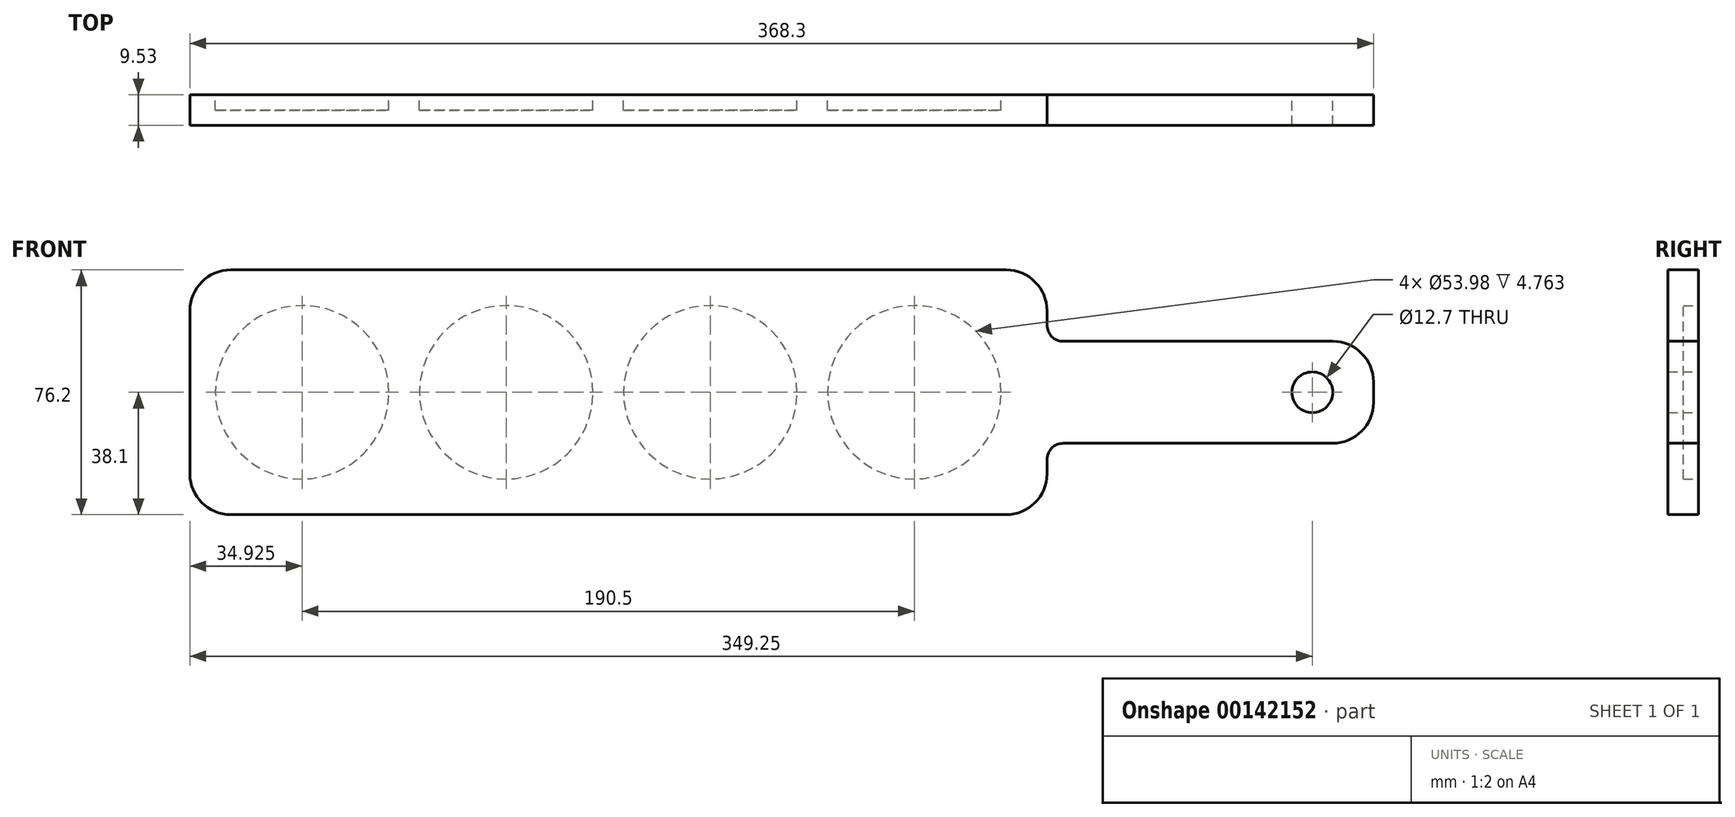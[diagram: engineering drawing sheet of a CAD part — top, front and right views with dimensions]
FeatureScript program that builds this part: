
annotation { "Feature Type Name" : "Feature", "Feature Type Description" : "" }
export const myFeature = defineFeature(function(context is Context, id is Id, definition is map)
    precondition{}
    {
        {
            var Q0;
            Q0=qCreatedBy(makeId("Front.planeOp"),FACE);
            var sketch = newSketch(context, id + "F0", { "sketchPlane" : qUnion([Q0])});
            skLineSegment(sketch, "E0.bottom", {"start": v(0, 0) * mm, "end": v(266.7, 0) * mm});
            skLineSegment(sketch, "E0.top", {"start": v(0, 76.2) * mm, "end": v(266.7, 76.2) * mm});
            skLineSegment(sketch, "E0.left", {"start": v(0, 0) * mm, "end": v(0, 76.2) * mm});
            skCircle(sketch, "E1", {"center": v(34.93, 38.1) * mm, "radius": 26.99 * mm});
            skPoint(sketch, "E1.centerSnap0", {"position": v(0, 38.1) * mm});
            skCircle(sketch, "E2.1.0.0", {"center": v(98.42, 38.1) * mm, "radius": 26.99 * mm});
            skCircle(sketch, "E2.2.0.0", {"center": v(161.93, 38.1) * mm, "radius": 26.99 * mm});
            skCircle(sketch, "E2.3.0.0", {"center": v(225.43, 38.1) * mm, "radius": 26.99 * mm});
            skLineSegment(sketch, "E2.direction1", {"start": v(34.93, 38.1) * mm, "end": v(98.42, 38.1) * mm, "construction": true});
            skLineSegment(sketch, "E3.bottom", {"start": v(368.3, 22.22) * mm, "end": v(266.7, 22.22) * mm});
            skLineSegment(sketch, "E3.top", {"start": v(368.3, 53.97) * mm, "end": v(266.7, 53.97) * mm});
            skLineSegment(sketch, "E3.left", {"start": v(368.3, 22.22) * mm, "end": v(368.3, 53.97) * mm});
            skPoint(sketch, "E3.middle", {"position": v(317.5, 38.1) * mm});
            skLineSegment(sketch, "E4", {"start": v(266.7, 53.98) * mm, "end": v(266.7, 76.2) * mm});
            skLineSegment(sketch, "E5", {"start": v(266.7, 22.23) * mm, "end": v(266.7, 0) * mm});
            skPoint(sketch, "E6.orphan", {"position": v(313.72, 76.2) * mm});
            skPoint(sketch, "E7.orphan", {"position": v(321.28, 0) * mm});
            skSolve(sketch);
        }
        {
            var Q0;
            Q0 = qSketchRegion(id + "F0", true);
            var Q1;
            Q1=makeQuery(id+"F0.imprint","IMPRINT",FACE,{"disambiguationData":[TD([[makeQuery(id+"F0.imprint","IMPRINT",EDGE,{"derivedFrom":sQuery(id+"F0.wireOp",EDGE,"E1")}),1.0]])]});
            var Q2;
            Q2=makeQuery(id+"F0.imprint","IMPRINT",FACE,{"disambiguationData":[TD([[makeQuery(id+"F0.imprint","IMPRINT",EDGE,{"derivedFrom":sQuery(id+"F0.wireOp",EDGE,"E2.1.0.0")}),1.0]])]});
            var Q3;
            Q3=makeQuery(id+"F0.imprint","IMPRINT",FACE,{"disambiguationData":[TD([[makeQuery(id+"F0.imprint","IMPRINT",EDGE,{"derivedFrom":sQuery(id+"F0.wireOp",EDGE,"E2.2.0.0")}),1.0]])]});
            var Q4;
            Q4=makeQuery(id+"F0.imprint","IMPRINT",FACE,{"disambiguationData":[TD([[makeQuery(id+"F0.imprint","IMPRINT",EDGE,{"derivedFrom":sQuery(id+"F0.wireOp",EDGE,"E2.3.0.0")}),1.0]])]});
            extrude(context, id + "F1", {"entities" : qUnion([Q0, Q1, Q2, Q3, Q4]), "depth" : 9.52 * mm});
        }
        {
            var Q0;
            Q0=makeQuery(id+"F0.imprint","IMPRINT",FACE,{"disambiguationData":[TD([[makeQuery(id+"F0.imprint","IMPRINT",EDGE,{"derivedFrom":sQuery(id+"F0.wireOp",EDGE,"E2.3.0.0")}),1.0]])]});
            var Q1;
            Q1=makeQuery(id+"F0.imprint","IMPRINT",FACE,{"disambiguationData":[TD([[makeQuery(id+"F0.imprint","IMPRINT",EDGE,{"derivedFrom":sQuery(id+"F0.wireOp",EDGE,"E2.2.0.0")}),1.0]])]});
            var Q2;
            Q2=makeQuery(id+"F0.imprint","IMPRINT",FACE,{"disambiguationData":[TD([[makeQuery(id+"F0.imprint","IMPRINT",EDGE,{"derivedFrom":sQuery(id+"F0.wireOp",EDGE,"E2.1.0.0")}),1.0]])]});
            var Q3;
            Q3=makeQuery(id+"F0.imprint","IMPRINT",FACE,{"disambiguationData":[TD([[makeQuery(id+"F0.imprint","IMPRINT",EDGE,{"derivedFrom":sQuery(id+"F0.wireOp",EDGE,"E1")}),1.0]])]});
            extrude(context, id + "F2", {"entities" : qUnion([Q0, Q1, Q2, Q3]), "operationType" : NewBodyOperationType.REMOVE, "depth" : 4.76 * mm});
        }
        {
            var Q0;
            Q0=makeQuery(id+"F1.opExtrude","SWEPT_EDGE",EDGE,{"disambiguationData":[OSD([sQuery(id+"F0.wireOp",EDGE,"E0.top"),sQuery(id+"F0.wireOp",EDGE,"E0.left")])]});
            var Q1;
            Q1=makeQuery(id+"F1.opExtrude","SWEPT_EDGE",EDGE,{"disambiguationData":[OSD([sQuery(id+"F0.wireOp",EDGE,"E0.bottom"),sQuery(id+"F0.wireOp",EDGE,"E0.left")])]});
            var Q2;
            Q2=makeQuery(id+"F1.opExtrude","SWEPT_EDGE",EDGE,{"disambiguationData":[OSD([sQuery(id+"F0.wireOp",EDGE,"E0.top"),sQuery(id+"F0.wireOp",EDGE,"E4")])]});
            var Q3;
            Q3=makeQuery(id+"F1.opExtrude","SWEPT_EDGE",EDGE,{"disambiguationData":[OSD([sQuery(id+"F0.wireOp",EDGE,"E0.bottom"),sQuery(id+"F0.wireOp",EDGE,"E5")])]});
            var Q4;
            Q4=makeQuery(id+"F1.opExtrude","SWEPT_EDGE",EDGE,{"disambiguationData":[OSD([sQuery(id+"F0.wireOp",EDGE,"E3.top"),sQuery(id+"F0.wireOp",EDGE,"E3.left")])]});
            var Q5;
            Q5=makeQuery(id+"F1.opExtrude","SWEPT_EDGE",EDGE,{"disambiguationData":[OSD([sQuery(id+"F0.wireOp",EDGE,"E3.bottom"),sQuery(id+"F0.wireOp",EDGE,"E3.left")])]});
            fillet(context, id + "F3", {"entities" : qUnion([Q0, Q1, Q2, Q3, Q4, Q5]), "radius" : 12.7 * mm, "tangentPropagation" : true, "allowEdgeOverflow" : false});
        }
        {
            var Q0;
            Q0=makeQuery(id+"F1.opExtrude","CAP_FACE",FACE,{"disambiguationData":[OSD([sQuery(id+"F0.wireOp",EDGE,"E0.bottom"),sQuery(id+"F0.wireOp",EDGE,"E0.top"),sQuery(id+"F0.wireOp",EDGE,"E0.left"),sQuery(id+"F0.wireOp",EDGE,"E3.bottom"),sQuery(id+"F0.wireOp",EDGE,"E3.top"),sQuery(id+"F0.wireOp",EDGE,"E3.left"),sQuery(id+"F0.wireOp",EDGE,"E4"),sQuery(id+"F0.wireOp",EDGE,"E5")])],"isStart":true});
            var sketch = newSketch(context, id + "F4", { "sketchPlane" : qUnion([Q0])});
            skCircle(sketch, "E8", {"center": v(-349.25, 38.1) * mm, "radius": 6.35 * mm});
            skPoint(sketch, "E9", {"position": v(-368.3, 38.1) * mm});
            skSolve(sketch);
        }
        {
            var Q0;
            Q0 = qSketchRegion(id + "F4", true);
            extrude(context, id + "F5", {"entities" : qUnion([Q0]), "operationType" : NewBodyOperationType.REMOVE, "endBound" : BoundingType.THROUGH_ALL, "oppositeDirection" : true, "depth" : 25.4 * mm});
        }
        {
            var Q0;
            Q0=makeQuery(id+"F1.opExtrude","SWEPT_EDGE",EDGE,{"disambiguationData":[OSD([sQuery(id+"F0.wireOp",EDGE,"E3.top"),sQuery(id+"F0.wireOp",EDGE,"E4")])]});
            var Q1;
            Q1=makeQuery(id+"F1.opExtrude","SWEPT_EDGE",EDGE,{"disambiguationData":[OSD([sQuery(id+"F0.wireOp",EDGE,"E3.bottom"),sQuery(id+"F0.wireOp",EDGE,"E5")])]});
            fillet(context, id + "F6", {"entities" : qUnion([Q0, Q1]), "radius" : 5.08 * mm, "tangentPropagation" : true, "allowEdgeOverflow" : false});
        }
    });
